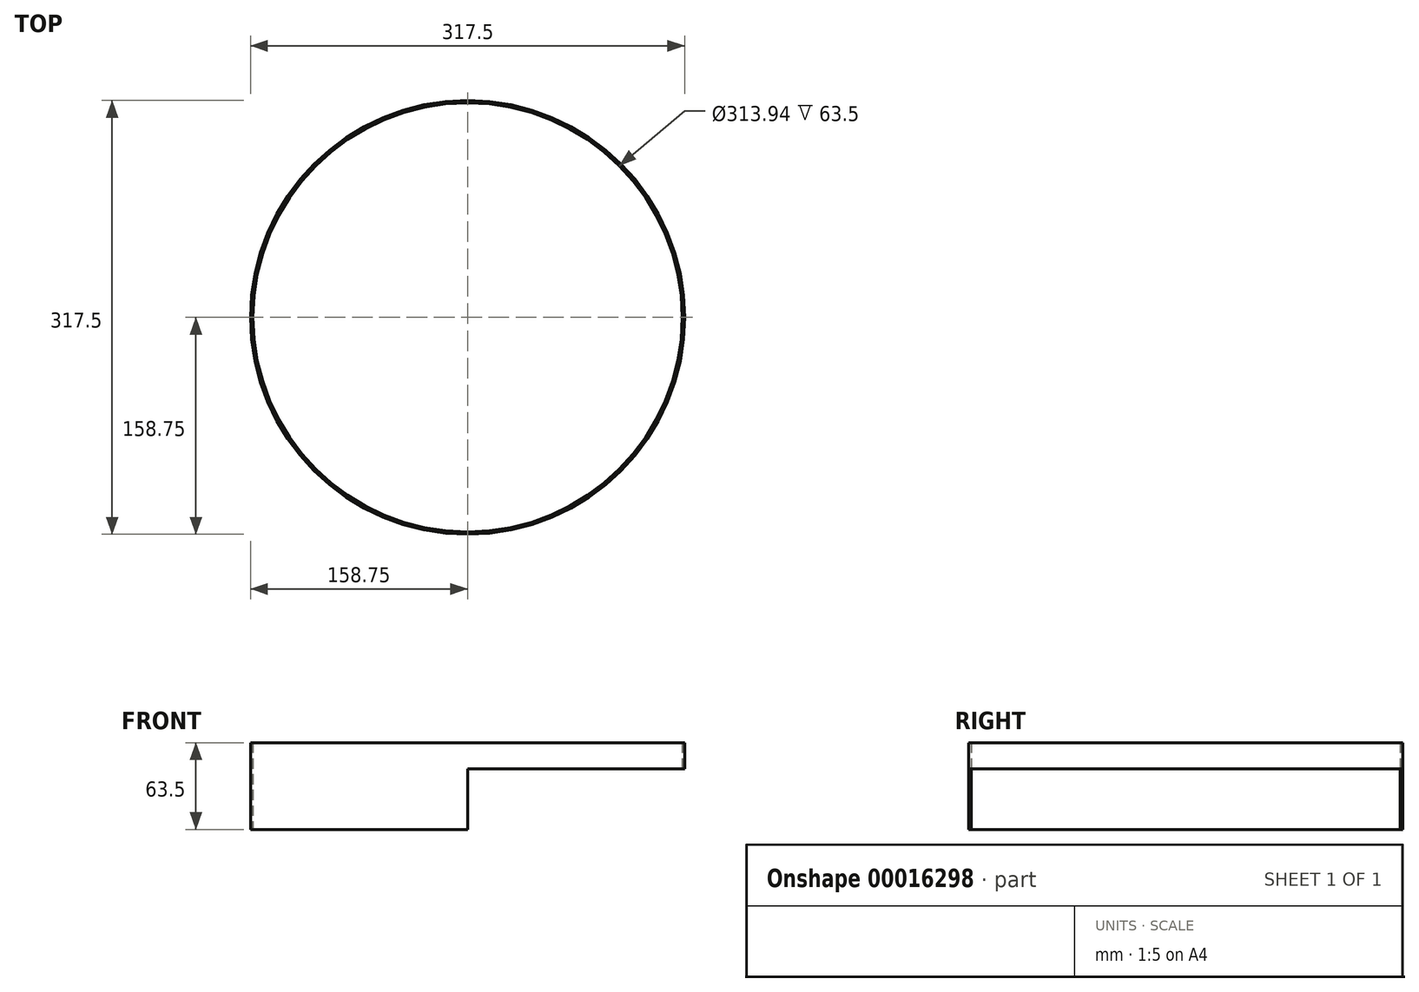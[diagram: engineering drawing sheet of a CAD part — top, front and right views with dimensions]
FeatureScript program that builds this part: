
annotation { "Feature Type Name" : "Feature", "Feature Type Description" : "" }
export const myFeature = defineFeature(function(context is Context, id is Id, definition is map)
    precondition{}
    {
        {
            var Q0;
            Q0=qCreatedBy(makeId("Top.planeOp"),FACE);
            var sketch = newSketch(context, id + "F0", { "sketchPlane" : qUnion([Q0])});
            skCircle(sketch, "E0", {"center": v(0, 0) * mm, "radius": 158.75 * mm});
            skCircle(sketch, "E1", {"center": v(0, 0) * mm, "radius": 156.97 * mm});
            skSolve(sketch);
        }
        {
            var Q0;
            Q0 = qSketchRegion(id + "F0", true);
            extrude(context, id + "F1", {"entities" : qUnion([Q0]), "depth" : 63.5 * mm});
        }
        {
            var Q0;
            Q0=qCreatedBy(makeId("Front.planeOp"),FACE);
            var sketch = newSketch(context, id + "F2", { "sketchPlane" : qUnion([Q0])});
            skLineSegment(sketch, "E2.bottom", {"start": v(0, 0) * mm, "end": v(177.8, 0) * mm});
            skLineSegment(sketch, "E2.top", {"start": v(0, 44.45) * mm, "end": v(177.8, 44.45) * mm});
            skLineSegment(sketch, "E2.left", {"start": v(0, 0) * mm, "end": v(0, 44.45) * mm});
            skLineSegment(sketch, "E2.right", {"start": v(177.8, 0) * mm, "end": v(177.8, 44.45) * mm});
            skSolve(sketch);
        }
        {
            var Q0;
            Q0 = qSketchRegion(id + "F2", true);
            extrude(context, id + "F3", {"entities" : qUnion([Q0]), "operationType" : NewBodyOperationType.REMOVE, "endBound" : BoundingType.SYMMETRIC, "oppositeDirection" : true, "depth" : 317.5 * mm});
        }
    });
